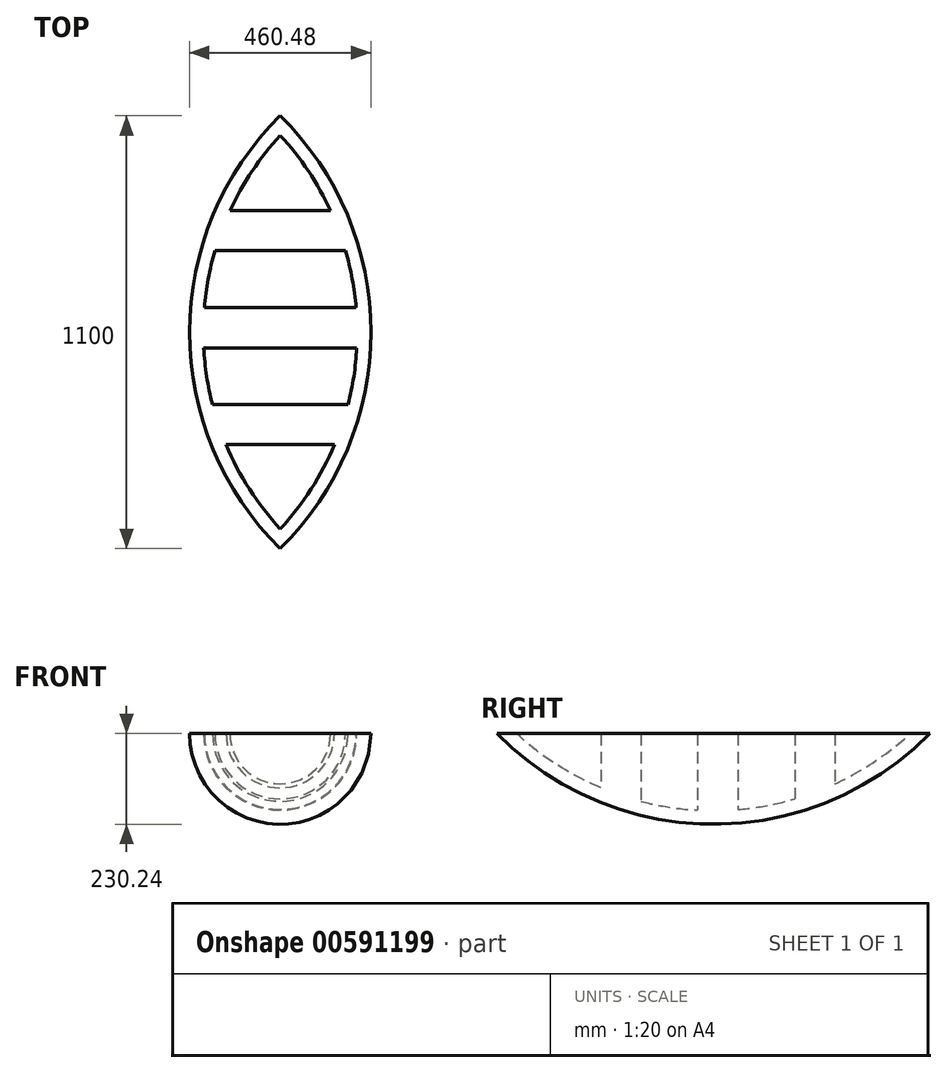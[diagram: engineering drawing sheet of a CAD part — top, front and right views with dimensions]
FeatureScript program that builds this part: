
annotation { "Feature Type Name" : "Feature", "Feature Type Description" : "" }
export const myFeature = defineFeature(function(context is Context, id is Id, definition is map)
    precondition{}
    {
        {
            var Q0;
            Q0=qCreatedBy(makeId("Top.planeOp"),FACE);
            var sketch = newSketch(context, id + "F0", { "sketchPlane" : qUnion([Q0])});
            skLineSegment(sketch, "E0", {"start": v(0, 0) * mm, "end": v(0, -50) * mm});
            skLineSegment(sketch, "E1", {"start": v(0, 1050) * mm, "end": v(0, 1000) * mm});
            skArc(sketch, "E2", {"start": v(0, -50) * mm, "mid": v(230.24, 500) * mm, "end": v(0, 1050) * mm});
            skArc(sketch, "E3", {"start": v(0, 0) * mm, "mid": v(78.17, 101.02) * mm, "end": v(137.73, 214.01) * mm});
            skLineSegment(sketch, "E4", {"start": v(137.73, 214.01) * mm, "end": v(0, 214.01) * mm});
            skLineSegment(sketch, "E5", {"start": v(0, 214.01) * mm, "end": v(0, 315.9) * mm});
            skLineSegment(sketch, "E6", {"start": v(0, 315.9) * mm, "end": v(172.1, 315.9) * mm});
            skPoint(sketch, "E7.orphan", {"position": v(175.32, 214.01) * mm});
            skArc(sketch, "E8.trimOffspring", {"start": v(172.1, 315.9) * mm, "mid": v(186.82, 387.5) * mm, "end": v(194.38, 460.23) * mm});
            skLineSegment(sketch, "E9", {"start": v(194.38, 460.23) * mm, "end": v(0, 460.23) * mm});
            skLineSegment(sketch, "E10", {"start": v(0, 460.23) * mm, "end": v(0, 562.11) * mm});
            skLineSegment(sketch, "E11", {"start": v(0, 562.11) * mm, "end": v(192.83, 562.11) * mm});
            skArc(sketch, "E12.trimOffspring", {"start": v(192.83, 562.11) * mm, "mid": v(182.98, 635.08) * mm, "end": v(165.89, 706.7) * mm});
            skLineSegment(sketch, "E13", {"start": v(127.77, 808.58) * mm, "end": v(0, 808.58) * mm});
            skLineSegment(sketch, "E14", {"start": v(0, 808.58) * mm, "end": v(0, 706.7) * mm});
            skLineSegment(sketch, "E15", {"start": v(0, 706.7) * mm, "end": v(165.89, 706.7) * mm});
            skArc(sketch, "E16.trimOffspring", {"start": v(127.77, 808.58) * mm, "mid": v(71.4, 909.3) * mm, "end": v(0, 1000) * mm});
            skSolve(sketch);
        }
        {
            var Q0;
            Q0=makeQuery(id+"F0.imprint","IMPRINT",FACE,{"disambiguationData":[TD([[makeQuery(id+"F0.imprint","IMPRINT",EDGE,{"derivedFrom":sQuery(id+"F0.wireOp",EDGE,"E0")}),1.0]])]});
            var Q1;
            Q1=sQuery(id+"F0.wireOp",EDGE,"E0");
            revolve(context, id + "F1", {"entities" : qUnion([Q0]), "axis" : qUnion([Q1]), "revolveType" : RevolveType.ONE_DIRECTION, "oppositeDirection" : true, "angle" : 180 * degree});
        }
    });
